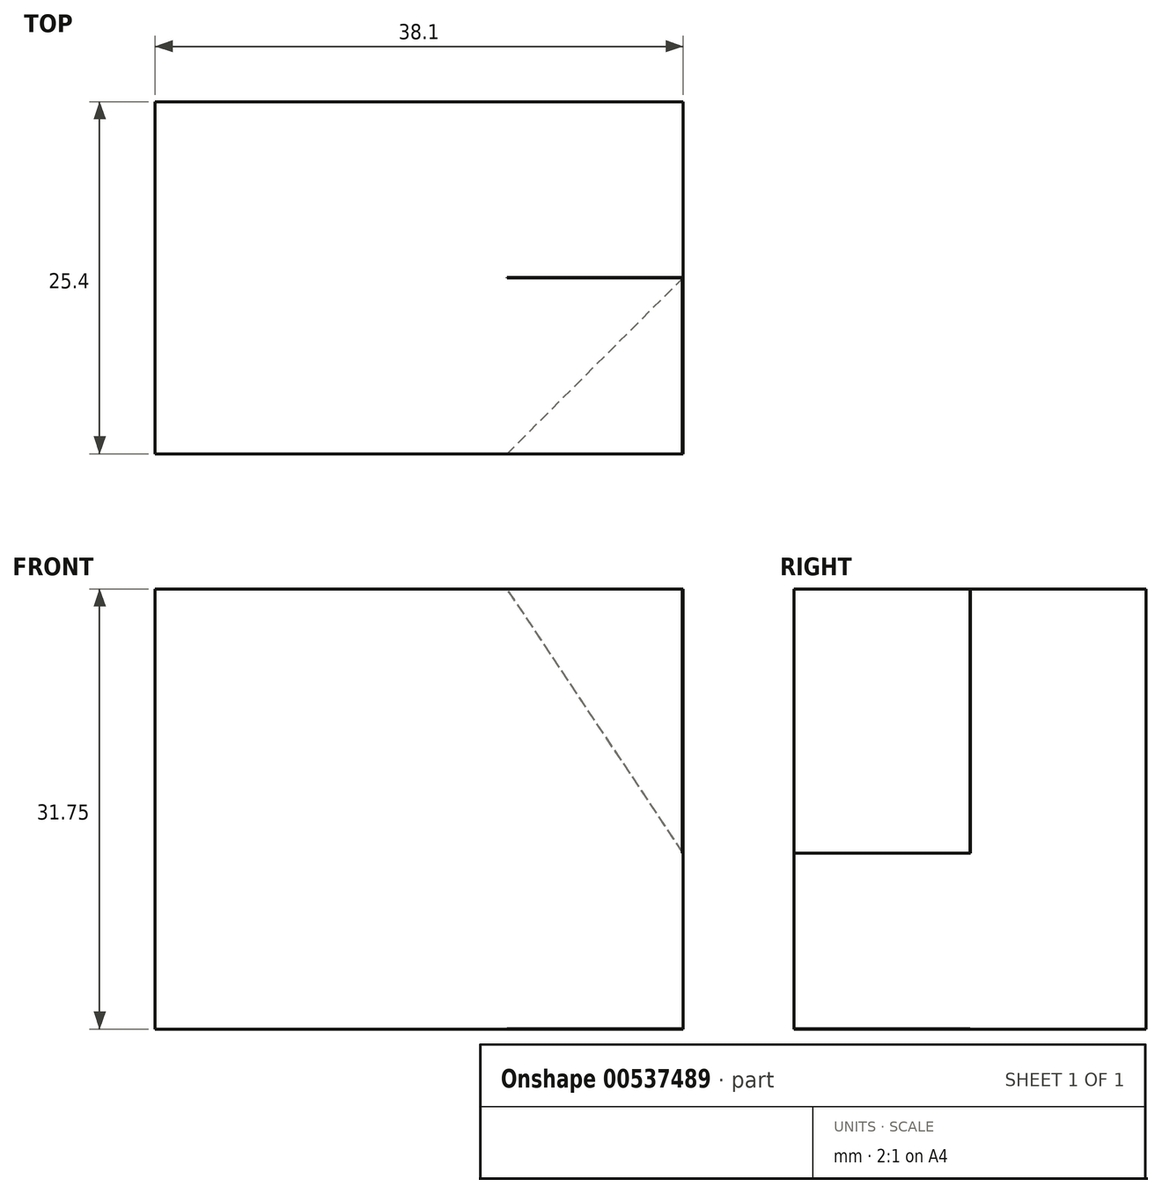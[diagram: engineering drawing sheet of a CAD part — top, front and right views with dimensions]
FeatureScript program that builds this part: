
annotation { "Feature Type Name" : "Feature", "Feature Type Description" : "" }
export const myFeature = defineFeature(function(context is Context, id is Id, definition is map)
    precondition{}
    {
        {
            var Q0;
            Q0=qCreatedBy(makeId("Front.planeOp"),FACE);
            var sketch = newSketch(context, id + "F0", { "sketchPlane" : qUnion([Q0])});
            skLineSegment(sketch, "E0", {"start": v(0, 0) * mm, "end": v(0, 31.75) * mm});
            skLineSegment(sketch, "E1", {"start": v(0, 31.75) * mm, "end": v(38.1, 31.75) * mm});
            skLineSegment(sketch, "E2", {"start": v(38.1, 31.75) * mm, "end": v(38.1, 0) * mm});
            skLineSegment(sketch, "E3", {"start": v(38.1, 0) * mm, "end": v(0, 0) * mm});
            skSolve(sketch);
        }
        {
            var Q0;
            Q0 = qSketchRegion(id + "F0", true);
            extrude(context, id + "F1", {"entities" : qUnion([Q0]), "depth" : 25.4 * mm, "offsetDistance" : 25.4 * mm});
        }
        {
            var Q0;
            Q0=makeQuery(id+"F1.opExtrude","SWEPT_FACE",FACE,{"disambiguationData":[OSD([sQuery(id+"F0.wireOp",EDGE,"E2")])]});
            var sketch = newSketch(context, id + "F2", { "sketchPlane" : qUnion([Q0])});
            skLineSegment(sketch, "E4", {"start": v(-25.4, 31.75) * mm, "end": v(-12.7, 31.75) * mm});
            skLineSegment(sketch, "E5", {"start": v(-12.7, 31.75) * mm, "end": v(-12.7, 12.7) * mm});
            skLineSegment(sketch, "E6", {"start": v(-12.7, 12.7) * mm, "end": v(-25.4, 12.7) * mm});
            skLineSegment(sketch, "E7", {"start": v(-25.4, 12.7) * mm, "end": v(-25.4, 31.75) * mm});
            skSolve(sketch);
        }
        {
            var Q0;
            Q0 = qSketchRegion(id + "F2", true);
            extrude(context, id + "F3", {"entities" : qUnion([Q0]), "operationType" : NewBodyOperationType.REMOVE, "oppositeDirection" : true, "depth" : 6 / 101.6 * mm, "offsetDistance" : 25.4 * mm});
        }
        {
            var Q0;
            Q0=makeQuery(id+"F1.opExtrude","SWEPT_FACE",FACE,{"disambiguationData":[OSD([sQuery(id+"F0.wireOp",EDGE,"E3")])]});
            var sketch = newSketch(context, id + "F4", { "sketchPlane" : qUnion([Q0])});
            skLineSegment(sketch, "E8", {"start": v(25.4, 25.4) * mm, "end": v(38.1, 25.4) * mm});
            skLineSegment(sketch, "E9", {"start": v(38.1, 25.4) * mm, "end": v(38.1, 12.7) * mm});
            skLineSegment(sketch, "E10", {"start": v(38.1, 12.7) * mm, "end": v(25.4, 25.4) * mm});
            skSolve(sketch);
        }
        {
            var Q0;
            Q0 = qSketchRegion(id + "F4", true);
            extrude(context, id + "F5", {"entities" : qUnion([Q0]), "operationType" : NewBodyOperationType.REMOVE, "oppositeDirection" : true, "depth" : 1 / 50.8 * mm, "offsetDistance" : 25.4 * mm});
        }
        {
            var Q0;
            Q0=makeQuery(id+"F3.boolean.opBoolean","COPY",FACE,{"derivedFrom":makeQuery(id+"F3.opExtrude","SWEPT_FACE",FACE,{"disambiguationData":[OSD([sQuery(id+"F2.wireOp",EDGE,"E5")])]})});
            var sketch = newSketch(context, id + "F6", { "sketchPlane" : qUnion([Q0])});
            skLineSegment(sketch, "E11", {"start": v(25.4, 31.75) * mm, "end": v(38.1, 31.75) * mm});
            skLineSegment(sketch, "E12", {"start": v(38.1, 31.75) * mm, "end": v(38.1, 12.7) * mm});
            skLineSegment(sketch, "E13", {"start": v(38.1, 12.7) * mm, "end": v(25.4, 31.75) * mm});
            skSolve(sketch);
        }
        {
            var Q0;
            Q0 = qSketchRegion(id + "F6", true);
            extrude(context, id + "F7", {"entities" : qUnion([Q0]), "operationType" : NewBodyOperationType.REMOVE, "oppositeDirection" : true, "depth" : 1 / 50.8 * mm, "offsetDistance" : 25.4 * mm});
        }
    });
